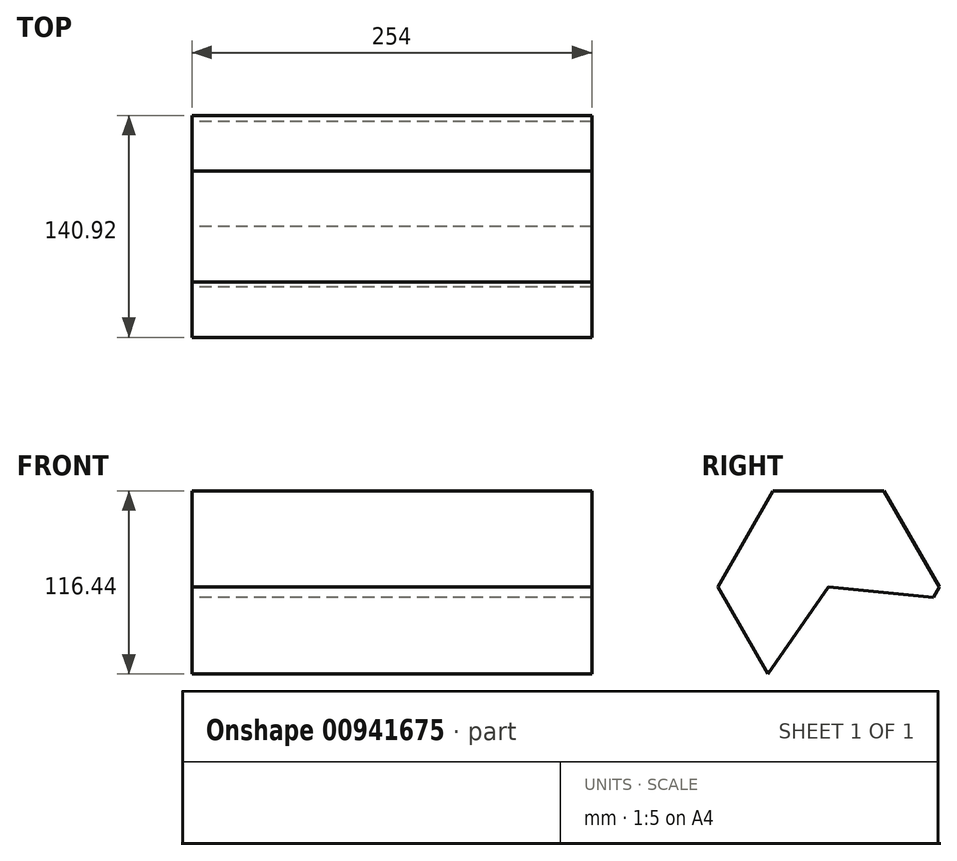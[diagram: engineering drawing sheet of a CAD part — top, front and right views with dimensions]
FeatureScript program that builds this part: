
annotation { "Feature Type Name" : "Feature", "Feature Type Description" : "" }
export const myFeature = defineFeature(function(context is Context, id is Id, definition is map)
    precondition{}
    {
        {
            var Q0;
            Q0=qCreatedBy(makeId("Right.planeOp"),FACE);
            var sketch = newSketch(context, id + "F0", { "sketchPlane" : qUnion([Q0])});
            skLineSegment(sketch, "E0", {"start": v(-115.93, 142.5) * mm, "end": v(-199.28, 22.42) * mm});
            skLineSegment(sketch, "E1", {"start": v(-199.28, 22.42) * mm, "end": v(0, 0) * mm});
            skLineSegment(sketch, "E2", {"start": v(0, 0) * mm, "end": v(62.8, 124.18) * mm});
            skLineSegment(sketch, "E3", {"start": v(62.8, 124.18) * mm, "end": v(-115.93, 142.5) * mm});
            skCircle(sketch, "E4.cCircle", {"center": v(-115.93, 142.5) * mm, "radius": 61.02 * mm, "construction": true});
            skLineSegment(sketch, "E4.0", {"start": v(-80.7, 203.53) * mm, "end": v(-45.47, 142.5) * mm});
            skLineSegment(sketch, "E4.1", {"start": v(-45.47, 142.5) * mm, "end": v(-80.7, 81.49) * mm});
            skLineSegment(sketch, "E4.2", {"start": v(-80.7, 81.49) * mm, "end": v(-151.16, 81.49) * mm});
            skLineSegment(sketch, "E4.3", {"start": v(-151.16, 81.49) * mm, "end": v(-186.4, 142.5) * mm});
            skLineSegment(sketch, "E4.4", {"start": v(-186.4, 142.5) * mm, "end": v(-151.16, 203.53) * mm});
            skLineSegment(sketch, "E4.5", {"start": v(-151.16, 203.53) * mm, "end": v(-80.7, 203.53) * mm});
            skPoint(sketch, "E4.0.midPoint", {"position": v(-63.09, 173.02) * mm});
            skSolve(sketch);
        }
        {
            var Q0;
            {var subQ1=sQuery(id+"F0.wireOp",EDGE,"E4.0");Q0=makeQuery(id+"F0.imprint","IMPRINT",FACE,{"disambiguationData":[TD([[makeQuery(id+"F0.imprint","IMPRINT",EDGE,{"derivedFrom":subQ1}),-1.0]])]});}
            extrude(context, id + "F1", {"entities" : qUnion([Q0]), "endBound" : BoundingType.SYMMETRIC, "depth" : 254 * mm, "offsetDistance" : 25.4 * mm});
        }
    });
